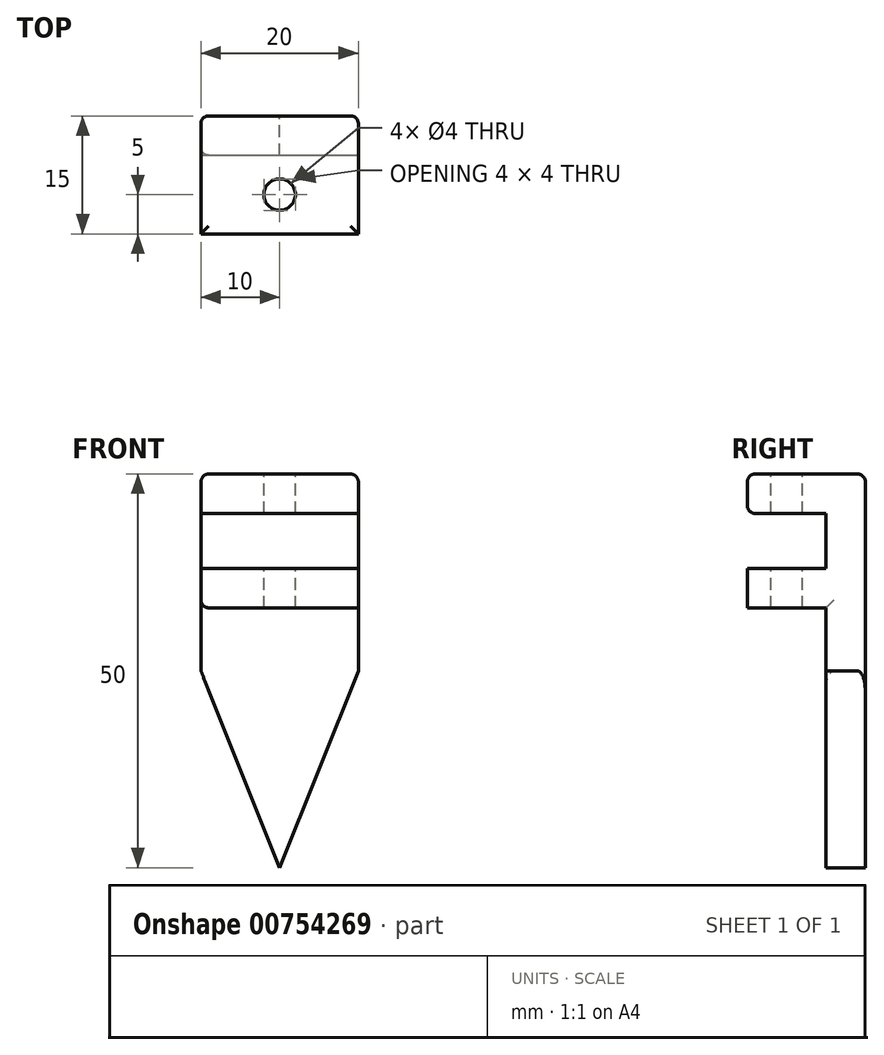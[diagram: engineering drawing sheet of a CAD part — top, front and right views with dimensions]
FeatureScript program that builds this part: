
annotation { "Feature Type Name" : "Feature", "Feature Type Description" : "" }
export const myFeature = defineFeature(function(context is Context, id is Id, definition is map)
    precondition{}
    {
        {
            var Q0;
            Q0=qCreatedBy(makeId("Front.planeOp"),FACE);
            var sketch = newSketch(context, id + "F0", { "sketchPlane" : qUnion([Q0])});
            skLineSegment(sketch, "E0.bottom", {"start": v(10, -25) * mm, "end": v(-10, -25) * mm});
            skLineSegment(sketch, "E0.top", {"start": v(10, 25) * mm, "end": v(-10, 25) * mm});
            skLineSegment(sketch, "E0.left", {"start": v(10, -25) * mm, "end": v(10, 25) * mm});
            skLineSegment(sketch, "E0.right", {"start": v(-10, -25) * mm, "end": v(-10, 25) * mm});
            skPoint(sketch, "E0.middle", {"position": v(0, 0) * mm});
            skSolve(sketch);
        }
        {
            var Q0;
            Q0=makeQuery(id+"F0.imprint","IMPRINT",FACE,{"disambiguationData":[TD([[makeQuery(id+"F0.imprint","IMPRINT",EDGE,{"derivedFrom":sQuery(id+"F0.wireOp",EDGE,"E0.bottom")}),-1.0]])]});
            extrude(context, id + "F1", {"entities" : qUnion([Q0]), "depth" : 15 * mm, "offsetDistance" : 25 * mm});
        }
        {
            var Q0;
            Q0=makeQuery(id+"F1.opExtrude","SWEPT_FACE",FACE,{"disambiguationData":[OSD([sQuery(id+"F0.wireOp",EDGE,"E0.left")])]});
            var sketch = newSketch(context, id + "F2", { "sketchPlane" : qUnion([Q0])});
            skLineSegment(sketch, "E1.bottom", {"start": v(-15, 20) * mm, "end": v(-5, 20) * mm});
            skLineSegment(sketch, "E1.top", {"start": v(-15, 13) * mm, "end": v(-5, 13) * mm});
            skLineSegment(sketch, "E1.left", {"start": v(-15, 20) * mm, "end": v(-15, 13) * mm});
            skLineSegment(sketch, "E1.right", {"start": v(-5, 20) * mm, "end": v(-5, 13) * mm});
            skLineSegment(sketch, "E2.bottom", {"start": v(-15, 8) * mm, "end": v(-5, 8) * mm});
            skLineSegment(sketch, "E2.top", {"start": v(-15, -25) * mm, "end": v(-5, -25) * mm});
            skLineSegment(sketch, "E2.left", {"start": v(-15, 8) * mm, "end": v(-15, -25) * mm});
            skLineSegment(sketch, "E2.right", {"start": v(-5, 8) * mm, "end": v(-5, -25) * mm});
            skSolve(sketch);
        }
        {
            var Q0;
            Q0=makeQuery(id+"F2.imprint","IMPRINT",FACE,{"disambiguationData":[TD([[makeQuery(id+"F2.imprint","IMPRINT",EDGE,{"derivedFrom":sQuery(id+"F2.wireOp",EDGE,"E1.bottom")}),-1.0]])]});
            var Q1;
            Q1=makeQuery(id+"F2.imprint","IMPRINT",FACE,{"disambiguationData":[TD([[makeQuery(id+"F2.imprint","IMPRINT",EDGE,{"derivedFrom":sQuery(id+"F2.wireOp",EDGE,"E2.bottom")}),-1.0]])]});
            extrude(context, id + "F3", {"entities" : qUnion([Q0, Q1]), "operationType" : NewBodyOperationType.REMOVE, "endBound" : BoundingType.THROUGH_ALL, "oppositeDirection" : true, "depth" : 25 * mm, "offsetDistance" : 25 * mm});
        }
        {
            var Q0;
            Q0=makeQuery(id+"F1.opExtrude","CAP_FACE",FACE,{"disambiguationData":[OSD([sQuery(id+"F0.wireOp",EDGE,"E0.bottom"),sQuery(id+"F0.wireOp",EDGE,"E0.top"),sQuery(id+"F0.wireOp",EDGE,"E0.left"),sQuery(id+"F0.wireOp",EDGE,"E0.right")])],"isStart":true});
            var sketch = newSketch(context, id + "F4", { "sketchPlane" : qUnion([Q0])});
            skLineSegment(sketch, "E3", {"start": v(-10, 0) * mm, "end": v(0, -25) * mm});
            skLineSegment(sketch, "E4", {"start": v(0, -25) * mm, "end": v(10, 0) * mm});
            skSolve(sketch);
        }
        {
            var Q0;
            {var subQ0=sQuery(id+"F4.wireOp",EDGE,"E3");Q0=makeQuery(id+"F4.imprint","IMPRINT",FACE,{"disambiguationData":[TD([[makeQuery(id+"F4.imprint","IMPRINT",EDGE,{"derivedFrom":subQ0}),-1.0]])]});}
            var Q1;
            {var subQ0=sQuery(id+"F4.wireOp",EDGE,"E4");Q1=makeQuery(id+"F4.imprint","IMPRINT",FACE,{"disambiguationData":[TD([[makeQuery(id+"F4.imprint","IMPRINT",EDGE,{"derivedFrom":subQ0}),-1.0]])]});}
            extrude(context, id + "F5", {"entities" : qUnion([Q0, Q1]), "operationType" : NewBodyOperationType.REMOVE, "endBound" : BoundingType.THROUGH_ALL, "oppositeDirection" : true, "depth" : 25 * mm, "offsetDistance" : 25 * mm});
        }
        {
            var Q0;
            Q0=makeQuery(id+"F1.opExtrude","SWEPT_FACE",FACE,{"disambiguationData":[OSD([sQuery(id+"F0.wireOp",EDGE,"E0.top")])]});
            var sketch = newSketch(context, id + "F6", { "sketchPlane" : qUnion([Q0])});
            skCircle(sketch, "E5", {"center": v(0, -10) * mm, "radius": 2 * mm});
            skSolve(sketch);
        }
        {
            var Q0;
            Q0=makeQuery(id+"F6.imprint","IMPRINT",FACE,{"disambiguationData":[TD([[makeQuery(id+"F6.imprint","IMPRINT",EDGE,{"derivedFrom":sQuery(id+"F6.wireOp",EDGE,"E5")}),1.0]])]});
            extrude(context, id + "F7", {"entities" : qUnion([Q0]), "operationType" : NewBodyOperationType.REMOVE, "endBound" : BoundingType.THROUGH_ALL, "oppositeDirection" : true, "depth" : 25 * mm, "offsetDistance" : 25 * mm});
        }
        {
            var Q0;
            Q0=makeQuery(id+"F1.opExtrude","CAP_EDGE",EDGE,{"disambiguationData":[OSD([sQuery(id+"F0.wireOp",EDGE,"E0.top")])],"isStart":true});
            var Q1;
            Q1=makeQuery(id+"F1.opExtrude","SWEPT_EDGE",EDGE,{"disambiguationData":[OSD([sQuery(id+"F0.wireOp",EDGE,"E0.top"),sQuery(id+"F0.wireOp",EDGE,"E0.left")])]});
            var Q2;
            Q2=makeQuery(id+"F1.opExtrude","SWEPT_EDGE",EDGE,{"disambiguationData":[OSD([sQuery(id+"F0.wireOp",EDGE,"E0.top"),sQuery(id+"F0.wireOp",EDGE,"E0.right")])]});
            var Q3;
            Q3=makeQuery(id+"F1.opExtrude","CAP_EDGE",EDGE,{"disambiguationData":[OSD([sQuery(id+"F0.wireOp",EDGE,"E0.top")])],"isStart":false});
            var Q4;
            Q4=makeQuery(id+"F1.opExtrude","CAP_EDGE",EDGE,{"disambiguationData":[OSD([sQuery(id+"F0.wireOp",EDGE,"E0.left")])],"isStart":true});
            var Q5;
            Q5=makeQuery(id+"F1.opExtrude","CAP_EDGE",EDGE,{"disambiguationData":[OSD([sQuery(id+"F0.wireOp",EDGE,"E0.right")])],"isStart":true});
            var Q6;
            Q6=makeQuery(id+"F3.boolean.opBoolean","INTERSECT",EDGE,{"derivedFrom":[makeQuery(id+"F1.opExtrude","SWEPT_FACE",FACE,{"disambiguationData":[OSD([sQuery(id+"F0.wireOp",EDGE,"E0.right")])]}),makeQuery(id+"F3.opExtrude","SWEPT_FACE",FACE,{"disambiguationData":[OSD([sQuery(id+"F2.wireOp",EDGE,"E2.bottom")])]})]});
            var Q7;
            Q7=makeQuery(id+"F3.boolean.opBoolean","COPY",EDGE,{"derivedFrom":makeQuery(id+"F3.opExtrude","CAP_EDGE",EDGE,{"disambiguationData":[OSD([sQuery(id+"F2.wireOp",EDGE,"E2.bottom")])],"isStart":true})});
            var Q8;
            Q8=makeQuery(id+"F3.boolean.opBoolean","COPY",EDGE,{"derivedFrom":makeQuery(id+"F3.opExtrude","SWEPT_EDGE",EDGE,{"disambiguationData":[OSD([sQuery(id+"F0.wireOp",EDGE,"E0.left"),sQuery(id+"F2.wireOp",EDGE,"E2.bottom"),sQuery(id+"F2.wireOp",EDGE,"E2.left")])]})});
            fillet(context, id + "F8", {"entities" : qUnion([Q0, Q1, Q2, Q3, Q4, Q5, Q6, Q7, Q8]), "radius" : 1 * mm, "tangentPropagation" : true, "allowEdgeOverflow" : false});
        }
        {
            var Q0;
            Q0=makeQuery(id+"F3.boolean.opBoolean","COPY",EDGE,{"derivedFrom":makeQuery(id+"F3.opExtrude","SWEPT_EDGE",EDGE,{"disambiguationData":[OSD([sQuery(id+"F0.wireOp",EDGE,"E0.left"),sQuery(id+"F2.wireOp",EDGE,"E1.top"),sQuery(id+"F2.wireOp",EDGE,"E1.left")])]})});
            var Q1;
            Q1=makeQuery(id+"F3.boolean.opBoolean","COPY",EDGE,{"derivedFrom":makeQuery(id+"F3.opExtrude","SWEPT_EDGE",EDGE,{"disambiguationData":[OSD([sQuery(id+"F0.wireOp",EDGE,"E0.left"),sQuery(id+"F2.wireOp",EDGE,"E1.bottom"),sQuery(id+"F2.wireOp",EDGE,"E1.left")])]})});
            var Q2;
            Q2=makeQuery(id+"F3.boolean.opBoolean","INTERSECT",EDGE,{"derivedFrom":[makeQuery(id+"F1.opExtrude","SWEPT_FACE",FACE,{"disambiguationData":[OSD([sQuery(id+"F0.wireOp",EDGE,"E0.right")])]}),makeQuery(id+"F3.opExtrude","SWEPT_FACE",FACE,{"disambiguationData":[OSD([sQuery(id+"F2.wireOp",EDGE,"E2.right")])]})]});
            var Q3;
            Q3=makeQuery(id+"F3.boolean.opBoolean","COPY",EDGE,{"derivedFrom":makeQuery(id+"F3.opExtrude","CAP_EDGE",EDGE,{"disambiguationData":[OSD([sQuery(id+"F2.wireOp",EDGE,"E2.right")])],"isStart":true})});
            fillet(context, id + "F9", {"entities" : qUnion([Q0, Q1, Q2, Q3]), "radius" : 1 * mm, "tangentPropagation" : true, "allowEdgeOverflow" : false});
        }
    });
